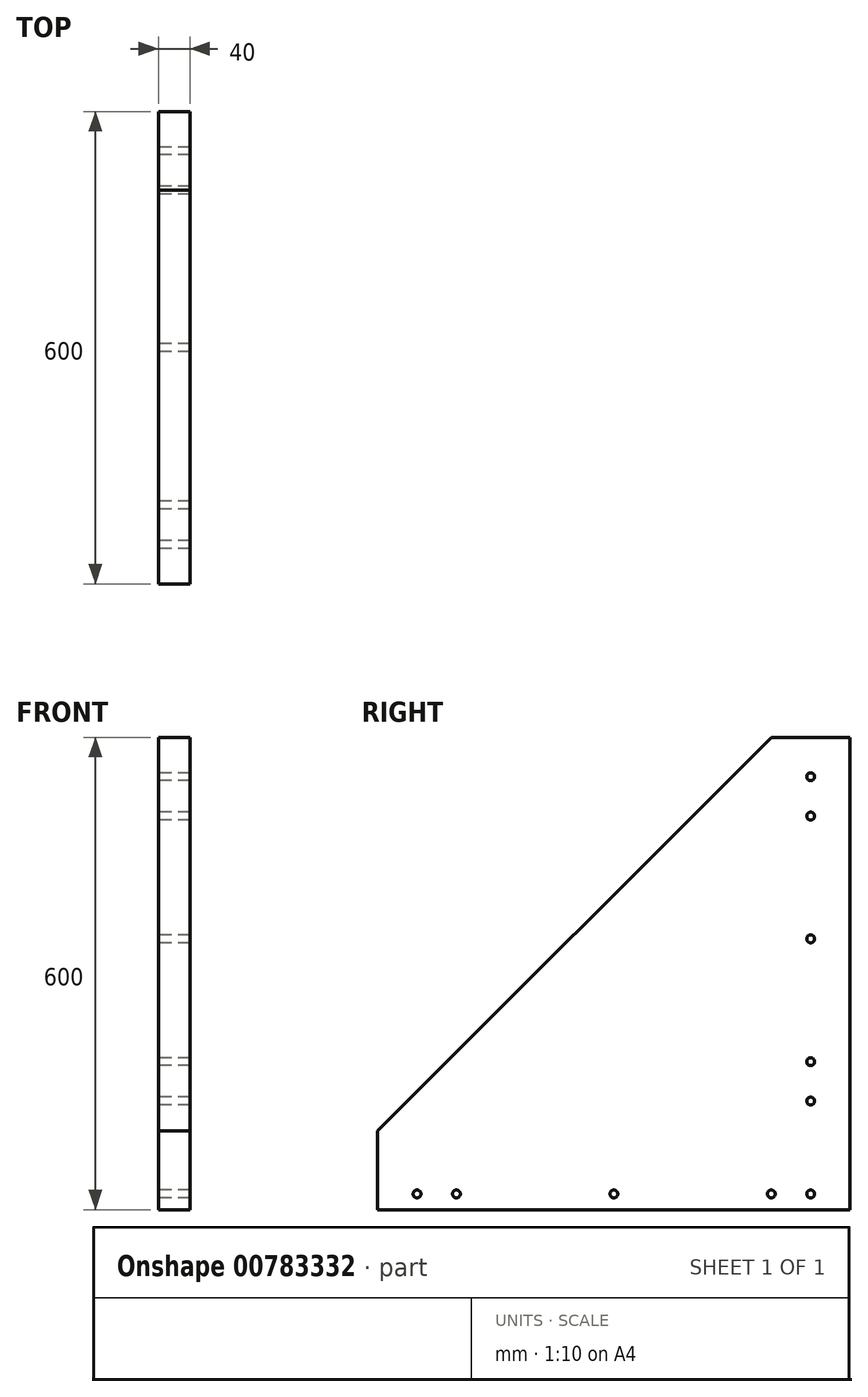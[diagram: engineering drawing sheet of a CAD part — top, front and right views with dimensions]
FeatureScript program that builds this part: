
annotation { "Feature Type Name" : "Feature", "Feature Type Description" : "" }
export const myFeature = defineFeature(function(context is Context, id is Id, definition is map)
    precondition{}
    {
        {
            var Q0;
            Q0=qCreatedBy(makeId("Right.planeOp"),FACE);
            var sketch = newSketch(context, id + "F0", { "sketchPlane" : qUnion([Q0])});
            skLineSegment(sketch, "E0.bottom", {"start": v(0, 0) * mm, "end": v(-600, 0) * mm});
            skLineSegment(sketch, "E0.top", {"start": v(0, 600) * mm, "end": v(-100, 600) * mm});
            skLineSegment(sketch, "E0.left", {"start": v(0, 0) * mm, "end": v(0, 600) * mm});
            skLineSegment(sketch, "E0.right", {"start": v(-600, 0) * mm, "end": v(-600, 100) * mm});
            skLineSegment(sketch, "E1", {"start": v(-100, 600) * mm, "end": v(-600, 600) * mm, "construction": true});
            skLineSegment(sketch, "E2", {"start": v(-600, 100) * mm, "end": v(-600, 600) * mm, "construction": true});
            skLineSegment(sketch, "E3", {"start": v(-100, 600) * mm, "end": v(-600, 100) * mm});
            skSolve(sketch);
        }
        {
            var Q0;
            Q0 = qSketchRegion(id + "F0", true);
            extrude(context, id + "F1", {"entities" : qUnion([Q0]), "depth" : 40 * mm, "offsetDistance" : 25 * mm});
        }
        {
            var Q0;
            Q0=makeQuery(id+"F1.opExtrude","CAP_FACE",FACE,{"disambiguationData":[OSD([sQuery(id+"F0.wireOp",EDGE,"E0.bottom"),sQuery(id+"F0.wireOp",EDGE,"E0.top"),sQuery(id+"F0.wireOp",EDGE,"E0.left"),sQuery(id+"F0.wireOp",EDGE,"E0.right"),sQuery(id+"F0.wireOp",EDGE,"E3")])],"isStart":true});
            var sketch = newSketch(context, id + "F2", { "sketchPlane" : qUnion([Q0])});
            skLineSegment(sketch, "E4", {"start": v(0, 20) * mm, "end": v(50, 20) * mm, "construction": true});
            skLineSegment(sketch, "E5", {"start": v(50, 20) * mm, "end": v(100, 20) * mm, "construction": true});
            skLineSegment(sketch, "E6", {"start": v(100, 20) * mm, "end": v(300, 20) * mm, "construction": true});
            skLineSegment(sketch, "E7", {"start": v(300, 20) * mm, "end": v(500, 20) * mm, "construction": true});
            skLineSegment(sketch, "E8", {"start": v(500, 20) * mm, "end": v(550, 20) * mm, "construction": true});
            skLineSegment(sketch, "E9", {"start": v(550, 20) * mm, "end": v(600, 20) * mm, "construction": true});
            skSolve(sketch);
        }
        {
            var Q0;
            Q0=makeQuery(id+"F2.imprint","IMPRINT",FACE,{"disambiguationData":[TD([[makeQuery(id+"F2.imprint","IMPRINT",EDGE,{"derivedFrom":makeQuery(id+"F1.opExtrude","CAP_EDGE",EDGE,{"disambiguationData":[OSD([sQuery(id+"F0.wireOp",EDGE,"E0.bottom")])],"isStart":true})}),1.0]])]});
            var sketch = newSketch(context, id + "F3", { "sketchPlane" : qUnion([Q0])});
            skLineSegment(sketch, "E10", {"start": v(50, 0) * mm, "end": v(50, 88) * mm, "construction": true});
            skLineSegment(sketch, "E11", {"start": v(50, 88) * mm, "end": v(50, 138) * mm, "construction": true});
            skLineSegment(sketch, "E12", {"start": v(50, 138) * mm, "end": v(50, 188) * mm, "construction": true});
            skLineSegment(sketch, "E13", {"start": v(50, 188) * mm, "end": v(50, 344) * mm, "construction": true});
            skLineSegment(sketch, "E14", {"start": v(50, 344) * mm, "end": v(50, 500) * mm, "construction": true});
            skLineSegment(sketch, "E15", {"start": v(50, 500) * mm, "end": v(50, 550) * mm, "construction": true});
            skLineSegment(sketch, "E16", {"start": v(50, 550) * mm, "end": v(50, 600) * mm, "construction": true});
            skSolve(sketch);
        }
        {
            var Q0;
            Q0=sQuery(id+"F2.wireOp",VERTEX,"E4.end");
            var Q1;
            Q1=sQuery(id+"F2.wireOp",VERTEX,"E5.end");
            var Q2;
            Q2=sQuery(id+"F2.wireOp",VERTEX,"E6.end");
            var Q3;
            Q3=sQuery(id+"F2.wireOp",VERTEX,"E7.end");
            var Q4;
            Q4=sQuery(id+"F2.wireOp",VERTEX,"E8.end");
            var Q5;
            Q5=sQuery(id+"F3.wireOp",VERTEX,"E11.end");
            var Q6;
            Q6=sQuery(id+"F3.wireOp",VERTEX,"E12.end");
            var Q7;
            Q7=sQuery(id+"F3.wireOp",VERTEX,"E13.end");
            var Q8;
            Q8=sQuery(id+"F3.wireOp",VERTEX,"E14.end");
            var Q9;
            Q9=sQuery(id+"F3.wireOp",VERTEX,"E15.end");
            var Q10;
            Q10=makeQuery(id+"F1.opExtrude","SWEPT_BODY",BODY,{"disambiguationData":[OSD([sQuery(id+"F0.wireOp",EDGE,"E0.bottom"),sQuery(id+"F0.wireOp",EDGE,"E0.top"),sQuery(id+"F0.wireOp",EDGE,"E0.left"),sQuery(id+"F0.wireOp",EDGE,"E0.right"),sQuery(id+"F0.wireOp",EDGE,"E3")])]});
            hole(context, id + "F4", {"style" : HoleStyle.SIMPLE, "endStyle" : HoleEndStyle.THROUGH, "holeDiameter" : 10 * mm, "majorDiameter" : 5 * mm, "isTappedThrough" : true, "tappedDepth" : 12 * mm, "tapClearance" : 3, "locations" : qUnion([Q0, Q1, Q2, Q3, Q4, Q5, Q6, Q7, Q8, Q9]), "scope" : qUnion([Q10])});
        }
    });
